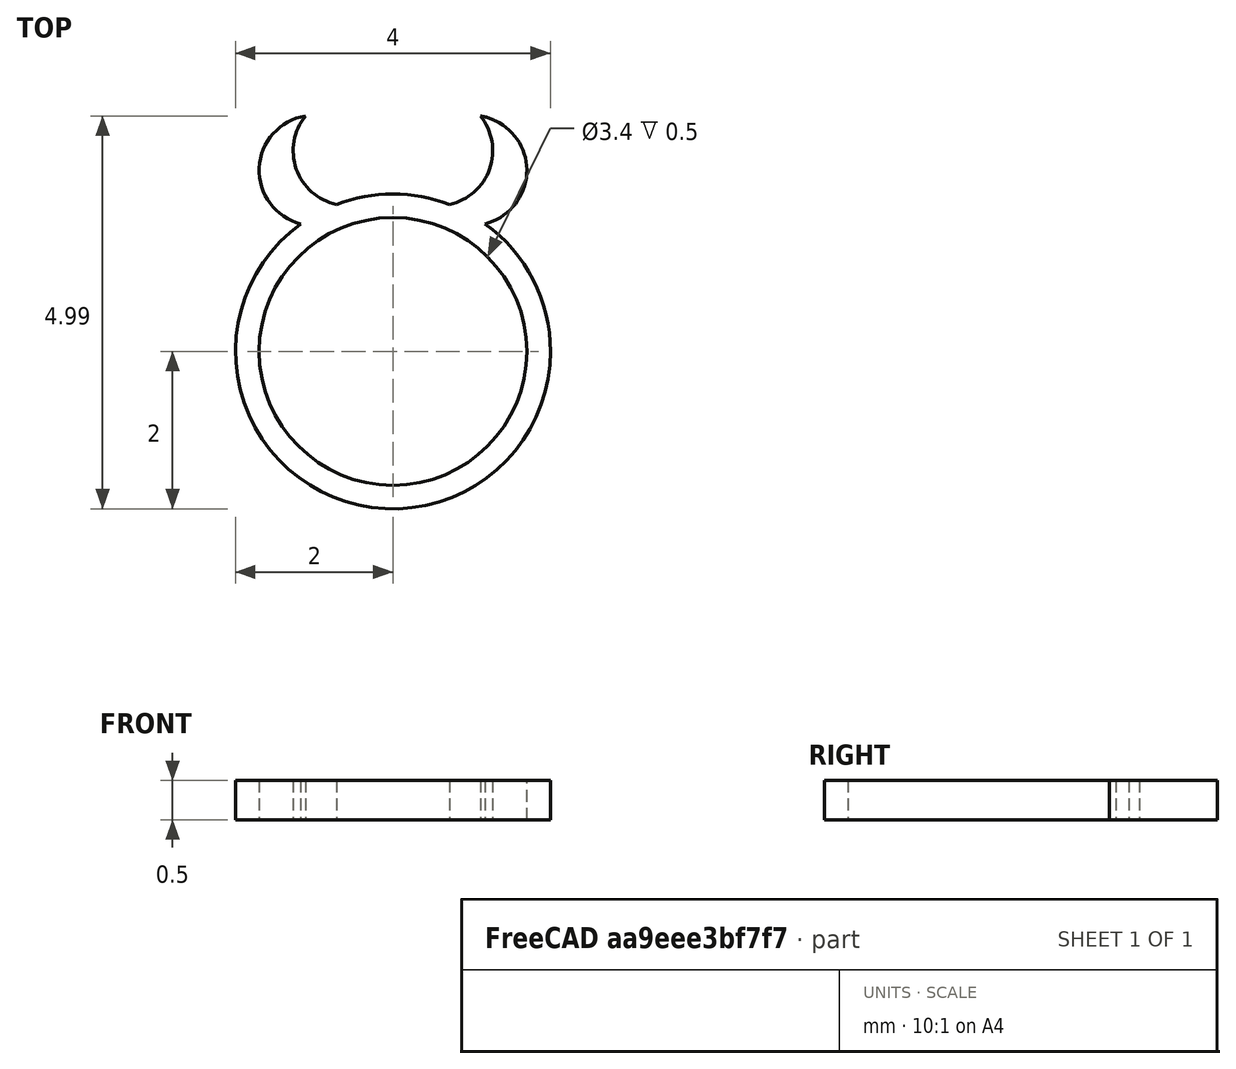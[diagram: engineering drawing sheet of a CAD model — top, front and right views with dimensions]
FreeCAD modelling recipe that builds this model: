
FCSTD DOCUMENT  (FreeCAD 0.20R29177 +233 (Git))
Label: anillo-diablillo
License: Creative Commons Attribution-ShareAlike
LicenseURL: http://creativecommons.org/licenses/by-sa/4.0/
objects: Part::Cylinder×6, Part::Cut×3, Part::MultiFuse×2
note: 11 computed .brp shape members not serialized (recipe doc carries the construction recipe); baked Part::Feature solids carry a one-line shape summary decoded from their .brp

FEATURE [Part::Cylinder] Cylinder  label="Cilindro"
  Angle = 360
  AttacherType = Attacher::AttachEngine3D
  FirstAngle = 0
  Height = 0.5
  Radius = 2
  SecondAngle = 0
FEATURE [Part::Cylinder] Cylinder001  label="Cilindro001"
  Angle = 360
  AttacherType = Attacher::AttachEngine3D
  FirstAngle = 0
  Height = 0.5
  Radius = 1.7
  SecondAngle = 0
FEATURE [Part::Cut] Cut
  Base = -> Cylinder
  Refine = true
  Tool = -> Cylinder001
FEATURE [Part::Cylinder] Cylinder002  label="Cilindro002"
  Angle = 360
  AttacherType = Attacher::AttachEngine3D
  FirstAngle = 0
  Height = 0.5
  Radius = 0.7
  SecondAngle = 0
FEATURE [Part::Cylinder] Cylinder003  label="Cilindro003"
  Angle = 360
  AttacherType = Attacher::AttachEngine3D
  FirstAngle = 0
  Height = 0.5
  Placement = pos=(0,0.5,0) rot=(0,0,1;0rad)
  Radius = 0.7
  SecondAngle = 0
FEATURE [Part::Cut] Cut001
  Base = -> Cylinder002
  Placement = pos=(1,2.3,0) rot=(0,0,1;1.0472rad)
  Refine = true
  Tool = -> Cylinder003
FEATURE [Part::Cylinder] Cylinder004  label="Cilindro004"
  Angle = 360
  AttacherType = Attacher::AttachEngine3D
  FirstAngle = 0
  Height = 0.5
  Radius = 0.7
  SecondAngle = 0
FEATURE [Part::Cylinder] Cylinder005  label="Cilindro005"
  Angle = 360
  AttacherType = Attacher::AttachEngine3D
  FirstAngle = 0
  Height = 0.5
  Placement = pos=(0,0.5,0) rot=(0,0,1;0rad)
  Radius = 0.7
  SecondAngle = 0
FEATURE [Part::Cut] Cut002
  Base = -> Cylinder004
  Placement = pos=(-1,2.3,0) rot=(0,0,1;-1.0472rad)
  Refine = true
  Tool = -> Cylinder005
FEATURE [Part::MultiFuse] Fusion
  Refine = true
  Shapes = -> [Cut,Cut001]
FEATURE [Part::MultiFuse] Fusion001
  Refine = true
  Shapes = -> [Cut002,Fusion]
